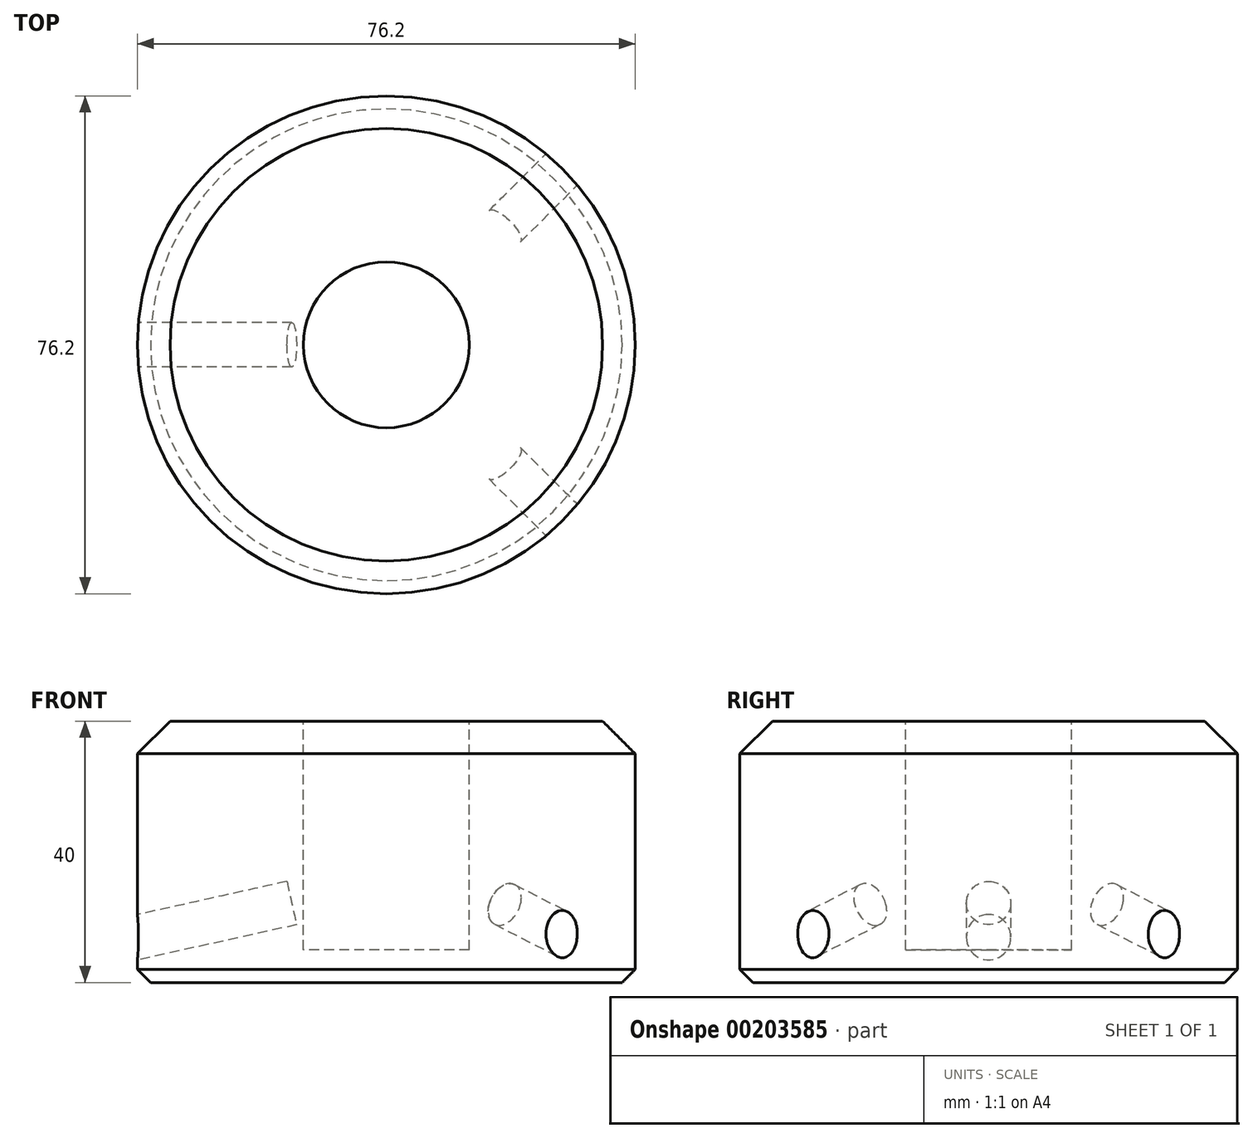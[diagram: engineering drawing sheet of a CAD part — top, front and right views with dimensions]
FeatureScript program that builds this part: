
annotation { "Feature Type Name" : "Feature", "Feature Type Description" : "" }
export const myFeature = defineFeature(function(context is Context, id is Id, definition is map)
    precondition{}
    {
        {
            var Q0;
            Q0=qCreatedBy(makeId("Top.planeOp"),FACE);
            var sketch = newSketch(context, id + "F0", { "sketchPlane" : qUnion([Q0])});
            skCircle(sketch, "E0", {"center": v(0, 0) * mm, "radius": 38.1 * mm});
            skSolve(sketch);
        }
        {
            var Q0;
            Q0=makeQuery(id+"F0.imprint","IMPRINT",FACE,{"disambiguationData":[TD([[makeQuery(id+"F0.imprint","IMPRINT",EDGE,{"derivedFrom":sQuery(id+"F0.wireOp",EDGE,"E0")}),1.0]])]});
            extrude(context, id + "F1", {"entities" : qUnion([Q0]), "depth" : 40 * mm});
        }
        {
            var Q0;
            Q0=makeQuery(id+"F1.opExtrude","CAP_FACE",FACE,{"disambiguationData":[OSD([sQuery(id+"F0.wireOp",EDGE,"E0")])],"isStart":false});
            var sketch = newSketch(context, id + "F2", { "sketchPlane" : qUnion([Q0])});
            skCircle(sketch, "E1", {"center": v(0, 0) * mm, "radius": 12.7 * mm});
            skSolve(sketch);
        }
        {
            var Q0;
            Q0 = qSketchRegion(id + "F2", true);
            extrude(context, id + "F3", {"entities" : qUnion([Q0]), "operationType" : NewBodyOperationType.REMOVE, "oppositeDirection" : true, "depth" : 35 * mm});
        }
        {
            var Q0;
            Q0=makeQuery(id+"F1.opExtrude","CAP_EDGE",EDGE,{"disambiguationData":[OSD([sQuery(id+"F0.wireOp",EDGE,"E0")])],"isStart":false});
            chamfer(context, id + "F4", {"entities" : qUnion([Q0]), "width" : 5 * mm, "tangentPropagation" : true});
        }
        {
            var Q0;
            Q0=qCreatedBy(makeId("Front.planeOp"),FACE);
            var Q1;
            Q1=qCreatedBy(makeId("Right.planeOp"),FACE);
            cPlane(context, id + "F5", {"entities" : qUnion([Q0, Q1]), "cplaneType" : CPlaneType.MID_PLANE, "offset" : 25 * mm, "width" : 150 * mm, "height" : 150 * mm});
        }
        {
            var Q0;
            Q0=qCreatedBy(makeId("Front.planeOp"),FACE);
            var Q1;
            Q1=qCreatedBy(makeId("Right.planeOp"),FACE);
            cPlane(context, id + "F6", {"entities" : qUnion([Q0, Q1]), "cplaneType" : CPlaneType.MID_PLANE, "offset" : 25 * mm, "flipAlignment" : true, "width" : 150 * mm, "height" : 150 * mm});
        }
        {
            var Q0;
            Q0=qCreatedBy(makeId("Front.planeOp"),FACE);
            var sketch = newSketch(context, id + "F7", { "sketchPlane" : qUnion([Q0])});
            skLineSegment(sketch, "E2", {"start": v(0, 0) * mm, "end": v(-60.04, -13.31) * mm, "construction": true});
            skLineSegment(sketch, "E3", {"start": v(0, 0) * mm, "end": v(0, 43.37) * mm, "construction": true});
            skLineSegment(sketch, "E4", {"start": v(0, 15.36) * mm, "end": v(-78.1, -1.95) * mm, "construction": true});
            skSolve(sketch);
        }
        {
            var Q0;
            Q0=sQuery(id+"F7.wireOp",EDGE,"E2");
            var Q1;
            Q1=sQuery(id+"F7.wireOp",VERTEX,"E2.end");
            cPlane(context, id + "F8", {"entities" : qUnion([Q0, Q1]), "cplaneType" : CPlaneType.LINE_POINT, "offset" : 25 * mm, "width" : 150 * mm, "height" : 150 * mm});
        }
        {
            var Q0;
            Q0=qCreatedBy(id+"F5.planeOp",FACE);
            var sketch = newSketch(context, id + "F9", { "sketchPlane" : qUnion([Q0])});
            skLineSegment(sketch, "E5", {"start": v(0, 0) * mm, "end": v(50.86, -18.51) * mm, "construction": true});
            skLineSegment(sketch, "E6.0", {"start": v(6.84, 18.8) * mm, "end": v(72.62, -5.15) * mm, "construction": true});
            skSolve(sketch);
        }
        {
            var Q0;
            Q0=sQuery(id+"F9.wireOp",EDGE,"E6.0");
            var Q1;
            Q1=sQuery(id+"F9.wireOp",VERTEX,"E6.0.end");
            cPlane(context, id + "F10", {"entities" : qUnion([Q0, Q1]), "cplaneType" : CPlaneType.LINE_POINT, "offset" : 25 * mm, "width" : 150 * mm, "height" : 150 * mm});
        }
        {
            var Q0;
            Q0=qCreatedBy(id+"F10.planeOp",FACE);
            var sketch = newSketch(context, id + "F11", { "sketchPlane" : qUnion([Q0])});
            skCircle(sketch, "E7", {"center": v(6.47, 18.92) * mm, "radius": 3.4 * mm});
            skSolve(sketch);
        }
        {
            var Q0;
            Q0=makeQuery(id+"F11.imprint","IMPRINT",FACE,{"disambiguationData":[TD([[makeQuery(id+"F11.imprint","IMPRINT",EDGE,{"derivedFrom":sQuery(id+"F11.wireOp",EDGE,"E7")}),1.0]])]});
            extrude(context, id + "F12", {"entities" : qUnion([Q0]), "operationType" : NewBodyOperationType.REMOVE, "oppositeDirection" : true, "depth" : 50 * mm});
        }
        {
            var Q0;
            Q0=qCreatedBy(id+"F6.planeOp",FACE);
            var sketch = newSketch(context, id + "F13", { "sketchPlane" : qUnion([Q0])});
            skLineSegment(sketch, "E8", {"start": v(0, 0) * mm, "end": v(62.4, -22.71) * mm, "construction": true});
            skLineSegment(sketch, "E9.0", {"start": v(6.84, 18.8) * mm, "end": v(72.62, -5.15) * mm, "construction": true});
            skSolve(sketch);
        }
        {
            var Q0;
            Q0=sQuery(id+"F13.wireOp",EDGE,"E9.0");
            var Q1;
            Q1=sQuery(id+"F13.wireOp",VERTEX,"E9.0.end");
            cPlane(context, id + "F14", {"entities" : qUnion([Q0, Q1]), "cplaneType" : CPlaneType.LINE_POINT, "offset" : 25 * mm, "width" : 150 * mm, "height" : 150 * mm});
        }
        {
            var Q0;
            Q0=makeQuery(id+"F1.opExtrude","CAP_EDGE",EDGE,{"disambiguationData":[OSD([sQuery(id+"F0.wireOp",EDGE,"E0")])],"isStart":true});
            chamfer(context, id + "F15", {"entities" : qUnion([Q0]), "width" : 2 * mm, "tangentPropagation" : true});
        }
        {
            var Q0;
            Q0=qCreatedBy(id+"F14.planeOp",FACE);
            var sketch = newSketch(context, id + "F16", { "sketchPlane" : qUnion([Q0])});
            skCircle(sketch, "E10", {"center": v(-6.47, 18.92) * mm, "radius": 3.4 * mm});
            skSolve(sketch);
        }
        {
            var Q0;
            Q0 = qSketchRegion(id + "F16", true);
            extrude(context, id + "F17", {"entities" : qUnion([Q0]), "operationType" : NewBodyOperationType.REMOVE, "oppositeDirection" : true, "depth" : 50 * mm});
        }
        {
            var Q0;
            Q0=qCreatedBy(id+"F8.planeOp",FACE);
            var sketch = newSketch(context, id + "F18", { "sketchPlane" : qUnion([Q0])});
            skCircle(sketch, "E11", {"center": v(0, 15) * mm, "radius": 3.4 * mm});
            skSolve(sketch);
        }
        {
            var Q0;
            Q0 = qSketchRegion(id + "F18", true);
            extrude(context, id + "F19", {"entities" : qUnion([Q0]), "operationType" : NewBodyOperationType.REMOVE, "oppositeDirection" : true, "depth" : 50 * mm});
        }
    });
